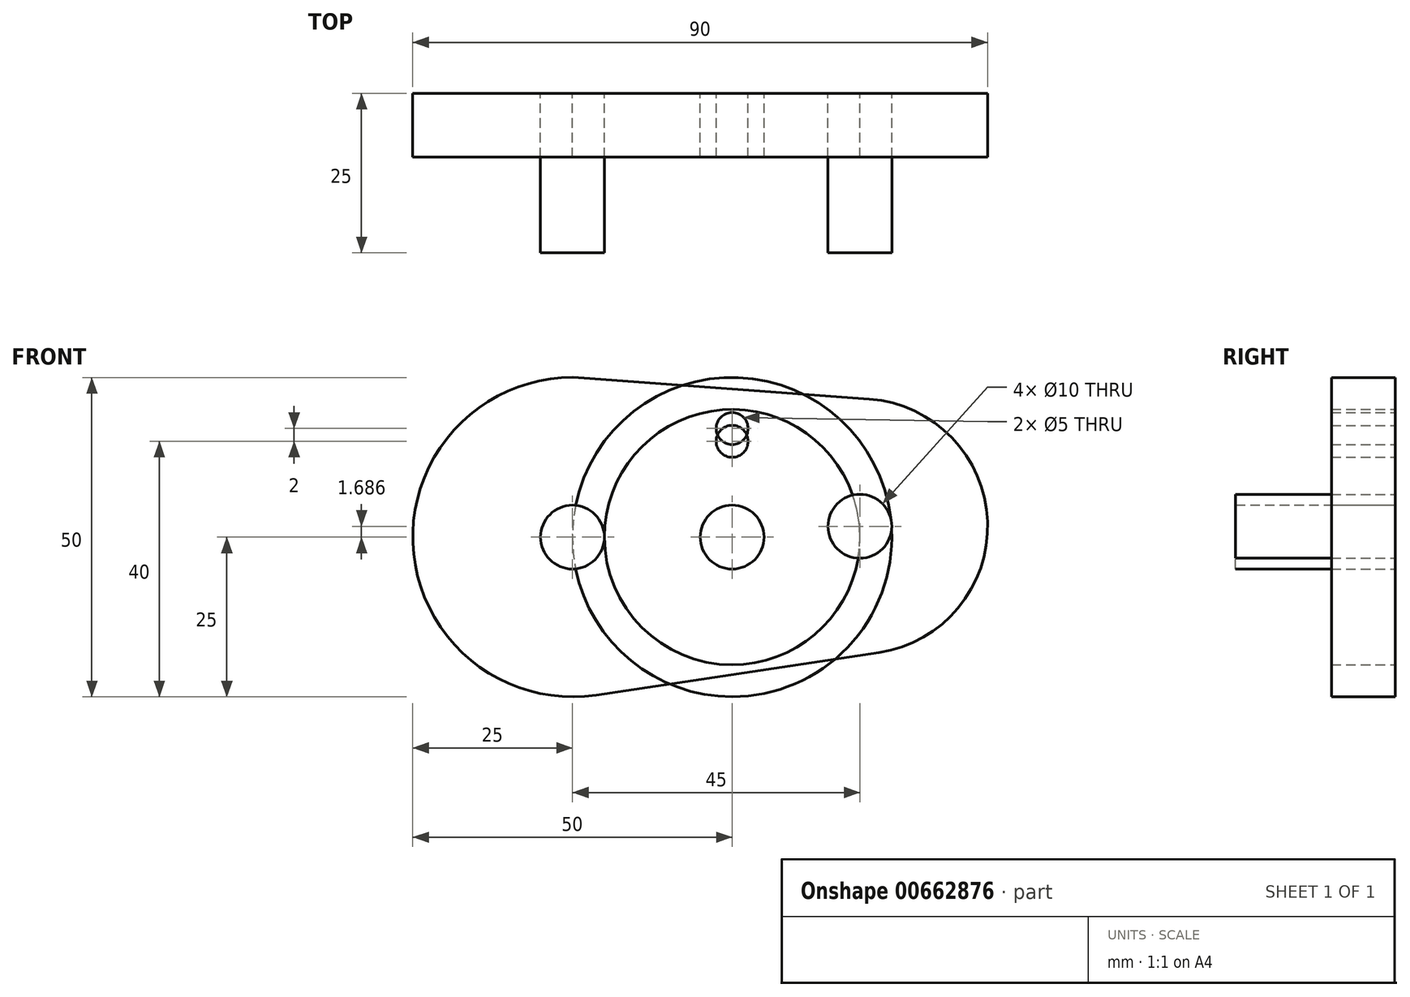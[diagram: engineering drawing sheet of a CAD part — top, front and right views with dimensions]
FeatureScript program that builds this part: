
annotation { "Feature Type Name" : "Feature", "Feature Type Description" : "" }
export const myFeature = defineFeature(function(context is Context, id is Id, definition is map)
    precondition{}
    {
        {
            var Q0;
            Q0=qCreatedBy(makeId("Front.planeOp"),FACE);
            var sketch = newSketch(context, id + "F0", { "sketchPlane" : qUnion([Q0])});
            skCircle(sketch, "E0", {"center": v(0, 0) * mm, "radius": 25 * mm});
            skCircle(sketch, "E1", {"center": v(0, 0) * mm, "radius": 5 * mm});
            skCircle(sketch, "E2", {"center": v(0, 17) * mm, "radius": 2.5 * mm});
            skSolve(sketch);
        }
        {
            var Q0;
            Q0 = qSketchRegion(id + "F0", true);
            extrude(context, id + "F1", {"entities" : qUnion([Q0]), "depth" : 25 * mm, "offsetDistance" : 25 * mm});
        }
        {
            var Q0;
            Q0=makeQuery(id+"F1.opExtrude","CAP_FACE",FACE,{"disambiguationData":[OSD([sQuery(id+"F0.wireOp",EDGE,"E0"),sQuery(id+"F0.wireOp",EDGE,"E1"),sQuery(id+"F0.wireOp",EDGE,"E2")])],"isStart":false});
            extrude(context, id + "F2", {"entities" : qUnion([Q0]), "operationType" : NewBodyOperationType.ADD, "oppositeDirection" : true, "depth" : 12.9 * mm, "offsetDistance" : 25 * mm});
        }
        {
            var Q0;
            Q0=makeQuery(id+"F1.opExtrude","CAP_FACE",FACE,{"disambiguationData":[OSD([sQuery(id+"F0.wireOp",EDGE,"E0"),sQuery(id+"F0.wireOp",EDGE,"E1"),sQuery(id+"F0.wireOp",EDGE,"E2")])],"isStart":false});
            extrude(context, id + "F3", {"entities" : qUnion([Q0]), "operationType" : NewBodyOperationType.REMOVE, "oppositeDirection" : true, "depth" : 15 * mm, "offsetDistance" : 25 * mm});
        }
        {
            var Q0;
            Q0=qCreatedBy(makeId("Front.planeOp"),FACE);
            var sketch = newSketch(context, id + "F4", { "sketchPlane" : qUnion([Q0])});
            skCircle(sketch, "E3", {"center": v(0, 0) * mm, "radius": 20 * mm});
            skCircle(sketch, "E4", {"center": v(0, 0) * mm, "radius": 5 * mm});
            skCircle(sketch, "E5", {"center": v(0, 15) * mm, "radius": 2.5 * mm});
            skSolve(sketch);
        }
        {
            var Q0;
            Q0 = qSketchRegion(id + "F4", true);
            extrude(context, id + "F5", {"entities" : qUnion([Q0]), "depth" : 25 * mm, "offsetDistance" : 25 * mm});
        }
        {
            var Q0;
            Q0=makeQuery(id+"F5.opExtrude","CAP_FACE",FACE,{"disambiguationData":[OSD([sQuery(id+"F4.wireOp",EDGE,"E3"),sQuery(id+"F4.wireOp",EDGE,"E4"),sQuery(id+"F4.wireOp",EDGE,"E5")])],"isStart":false});
            extrude(context, id + "F6", {"entities" : qUnion([Q0]), "operationType" : NewBodyOperationType.REMOVE, "oppositeDirection" : true, "depth" : 15 * mm, "offsetDistance" : 25 * mm});
        }
        {
            var Q0;
            Q0=qCreatedBy(makeId("Front.planeOp"),FACE);
            var sketch = newSketch(context, id + "F7", { "sketchPlane" : qUnion([Q0])});
            skLineSegment(sketch, "E6", {"start": v(-25, 29.87) * mm, "end": v(-25, -25.88) * mm, "construction": true});
            skArc(sketch, "E7", {"start": v(-23.16, 24.93) * mm, "mid": v(-49.98, -0.94) * mm, "end": v(-21.3, -24.72) * mm});
            skPoint(sketch, "E8.center.orphan", {"position": v(0, 0) * mm});
            skLineSegment(sketch, "E9", {"start": v(20, 28.71) * mm, "end": v(20, -25.34) * mm, "construction": true});
            skArc(sketch, "E10", {"start": v(20, -18.31) * mm, "mid": v(40, 1.69) * mm, "end": v(20, 21.69) * mm});
            skCircle(sketch, "E11", {"center": v(-25, 0) * mm, "radius": 5 * mm});
            skCircle(sketch, "E12", {"center": v(20, 1.69) * mm, "radius": 5 * mm});
            skLineSegment(sketch, "E13", {"start": v(-21.3, -24.72) * mm, "end": v(22.96, -18.1) * mm});
            skLineSegment(sketch, "E14", {"start": v(-23.16, 24.93) * mm, "end": v(21.47, 21.63) * mm});
            skSolve(sketch);
        }
        {
            var Q0;
            Q0=makeQuery(id+"F7.imprint","IMPRINT",FACE,{"disambiguationData":[TD([[makeQuery(id+"F7.imprint","IMPRINT",EDGE,{"derivedFrom":sQuery(id+"F7.wireOp",EDGE,"E12")}),1.0]])]});
            var Q1;
            Q1=makeQuery(id+"F7.imprint","IMPRINT",FACE,{"disambiguationData":[TD([[makeQuery(id+"F7.imprint","IMPRINT",EDGE,{"derivedFrom":sQuery(id+"F7.wireOp",EDGE,"E11")}),1.0]])]});
            extrude(context, id + "F8", {"entities" : qUnion([Q0, Q1]), "depth" : 25 * mm, "offsetDistance" : 25 * mm});
        }
        {
            var Q0;
            Q0=makeQuery(id+"F7.imprint","IMPRINT",FACE,{"disambiguationData":[TD([[makeQuery(id+"F7.imprint","IMPRINT",EDGE,{"derivedFrom":sQuery(id+"F7.wireOp",EDGE,"E7")}),1.0]])]});
            extrude(context, id + "F9", {"entities" : qUnion([Q0]), "depth" : 10 * mm, "offsetDistance" : 25 * mm});
        }
    });
